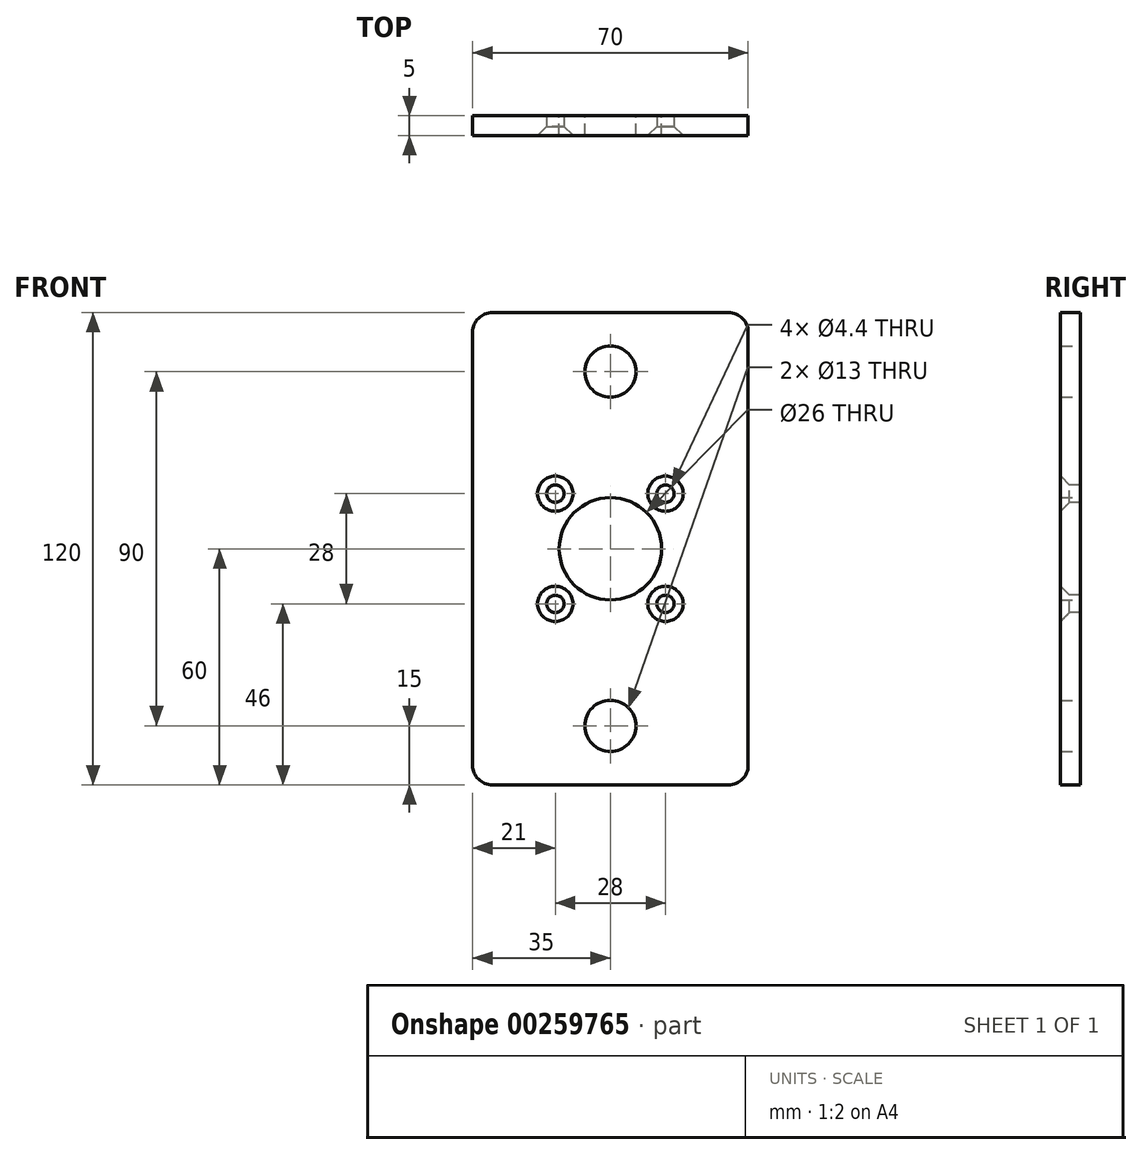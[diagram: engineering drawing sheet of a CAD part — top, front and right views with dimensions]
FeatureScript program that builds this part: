
annotation { "Feature Type Name" : "Feature", "Feature Type Description" : "" }
export const myFeature = defineFeature(function(context is Context, id is Id, definition is map)
    precondition{}
    {
        {
            var Q0;
            Q0=qCreatedBy(makeId("Front.planeOp"),FACE);
            var sketch = newSketch(context, id + "F0", { "sketchPlane" : qUnion([Q0])});
            skLineSegment(sketch, "E0.bottom", {"start": v(-35, 60) * mm, "end": v(35, 60) * mm});
            skLineSegment(sketch, "E0.top", {"start": v(-35, -60) * mm, "end": v(35, -60) * mm});
            skLineSegment(sketch, "E0.left", {"start": v(-35, 60) * mm, "end": v(-35, -60) * mm});
            skLineSegment(sketch, "E0.right", {"start": v(35, 60) * mm, "end": v(35, -60) * mm});
            skPoint(sketch, "E0.middle", {"position": v(0, 0) * mm});
            skCircle(sketch, "E1", {"center": v(0, 0) * mm, "radius": 13 * mm});
            skCircle(sketch, "E2", {"center": v(0, 45) * mm, "radius": 6.5 * mm});
            skCircle(sketch, "E3", {"center": v(0, -45) * mm, "radius": 6.5 * mm});
            skSolve(sketch);
        }
        {
            var Q0;
            Q0=makeQuery(id+"F0.imprint","IMPRINT",FACE,{"disambiguationData":[TD([[makeQuery(id+"F0.imprint","IMPRINT",EDGE,{"derivedFrom":sQuery(id+"F0.wireOp",EDGE,"E0.bottom")}),-1.0]])]});
            var Q1;
            Q1=makeQuery(id+"F0.imprint","IMPRINT",FACE,{"disambiguationData":[TD([[makeQuery(id+"F0.imprint","IMPRINT",EDGE,{"derivedFrom":sQuery(id+"F0.wireOp",EDGE,"3uLrPHQB-cvo3-0hqW-xmFe-uHz3Ib2TnryH")}),1.0]])]});
            var Q2;
            Q2=makeQuery(id+"F0.imprint","IMPRINT",FACE,{"disambiguationData":[TD([[makeQuery(id+"F0.imprint","IMPRINT",EDGE,{"derivedFrom":sQuery(id+"F0.wireOp",EDGE,"dDerD4UK-4sX2-t5OW-6pSG-Ia2GU2bfrqVv")}),1.0]])]});
            var Q3;
            Q3=makeQuery(id+"F0.imprint","IMPRINT",FACE,{"disambiguationData":[TD([[makeQuery(id+"F0.imprint","IMPRINT",EDGE,{"derivedFrom":sQuery(id+"F0.wireOp",EDGE,"HWgq7Ylu-Tews-VyOq-zJNp-kVzallqL1kV4")}),1.0]])]});
            var Q4;
            Q4=makeQuery(id+"F0.imprint","IMPRINT",FACE,{"disambiguationData":[TD([[makeQuery(id+"F0.imprint","IMPRINT",EDGE,{"derivedFrom":sQuery(id+"F0.wireOp",EDGE,"NZ8moLW7-Jqgc-e3bV-ixmb-ffZQiP1dNimV")}),1.0]])]});
            extrude(context, id + "F1", {"entities" : qUnion([Q0, Q1, Q2, Q3, Q4]), "depth" : 5 * mm});
        }
        {
            var Q0;
            Q0=makeQuery(id+"F1.opExtrude","CAP_FACE",FACE,{"disambiguationData":[OSD([sQuery(id+"F0.wireOp",EDGE,"E0.bottom"),sQuery(id+"F0.wireOp",EDGE,"E0.top"),sQuery(id+"F0.wireOp",EDGE,"E0.left"),sQuery(id+"F0.wireOp",EDGE,"E0.right"),sQuery(id+"F0.wireOp",EDGE,"E1"),sQuery(id+"F0.wireOp",EDGE,"E2"),sQuery(id+"F0.wireOp",EDGE,"E3")])],"isStart":false});
            var sketch = newSketch(context, id + "F2", { "sketchPlane" : qUnion([Q0])});
            skCircle(sketch, "E4", {"center": v(-14, 14) * mm, "radius": 2.2 * mm});
            skCircle(sketch, "E5", {"center": v(14, 14) * mm, "radius": 2.2 * mm});
            skCircle(sketch, "E6", {"center": v(14, -14) * mm, "radius": 2.2 * mm});
            skCircle(sketch, "E7", {"center": v(-14, -14) * mm, "radius": 2.2 * mm});
            skLineSegment(sketch, "E8", {"start": v(0, 0) * mm, "end": v(0, 26.65) * mm});
            skLineSegment(sketch, "E9", {"start": v(0, 26.65) * mm, "end": v(0, 0) * mm});
            skLineSegment(sketch, "E10", {"start": v(0, 0) * mm, "end": v(25.9, 0) * mm});
            skLineSegment(sketch, "E11", {"start": v(0, 0) * mm, "end": v(0, -25.46) * mm});
            skLineSegment(sketch, "E12", {"start": v(0, 0) * mm, "end": v(-25.6, 0) * mm});
            skSolve(sketch);
        }
        {
            var Q0;
            Q0=sQuery(id+"F2.wireOp",VERTEX,"E5.center");
            var Q1;
            Q1=sQuery(id+"F2.wireOp",VERTEX,"E4.center");
            var Q2;
            Q2=sQuery(id+"F2.wireOp",VERTEX,"E7.center");
            var Q3;
            Q3=sQuery(id+"F2.wireOp",VERTEX,"E6.center");
            var Q4;
            Q4=makeQuery(id+"F1.opExtrude","SWEPT_BODY",BODY,{"disambiguationData":[OSD([sQuery(id+"F0.wireOp",EDGE,"E0.bottom"),sQuery(id+"F0.wireOp",EDGE,"E0.top"),sQuery(id+"F0.wireOp",EDGE,"E0.left"),sQuery(id+"F0.wireOp",EDGE,"E0.right"),sQuery(id+"F0.wireOp",EDGE,"E1"),sQuery(id+"F0.wireOp",EDGE,"E2"),sQuery(id+"F0.wireOp",EDGE,"E3")])]});
            hole(context, id + "F3", {"style" : HoleStyle.C_SINK, "endStyle" : HoleEndStyle.BLIND, "standardTappedOrClearance" : lookupTablePath({ "standard" : "ISO", "fit" : "Normal", "size" : "M4", "type" : "Clearance" }), "standardBlindInLast" : lookupTablePath({ "fit" : "Standard", "standard" : "ISO", "size" : "M4", "type" : "Clearance" }), "holeDiameter" : 4.4 * mm, "cSinkDiameter" : 8.96 * mm, "cSinkAngle" : 90 * degree, "holeDepth" : 10 * mm, "tappedDepth" : 12 * mm, "tapClearance" : 3, "startFromSketch" : true, "locations" : qUnion([Q0, Q1, Q2, Q3]), "scope" : qUnion([Q4])});
        }
        {
            var Q0;
            Q0=makeQuery(id+"F1.opExtrude","SWEPT_EDGE",EDGE,{"disambiguationData":[OSD([sQuery(id+"F0.wireOp",EDGE,"E0.bottom"),sQuery(id+"F0.wireOp",EDGE,"E0.right")])]});
            var Q1;
            Q1=makeQuery(id+"F1.opExtrude","SWEPT_EDGE",EDGE,{"disambiguationData":[OSD([sQuery(id+"F0.wireOp",EDGE,"E0.top"),sQuery(id+"F0.wireOp",EDGE,"E0.right")])]});
            var Q2;
            Q2=makeQuery(id+"F1.opExtrude","SWEPT_EDGE",EDGE,{"disambiguationData":[OSD([sQuery(id+"F0.wireOp",EDGE,"E0.top"),sQuery(id+"F0.wireOp",EDGE,"E0.left")])]});
            var Q3;
            Q3=makeQuery(id+"F1.opExtrude","SWEPT_EDGE",EDGE,{"disambiguationData":[OSD([sQuery(id+"F0.wireOp",EDGE,"E0.bottom"),sQuery(id+"F0.wireOp",EDGE,"E0.left")])]});
            fillet(context, id + "F4", {"entities" : qUnion([Q0, Q1, Q2, Q3]), "radius" : 5 * mm, "tangentPropagation" : true, "allowEdgeOverflow" : false});
        }
    });
